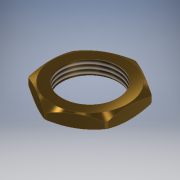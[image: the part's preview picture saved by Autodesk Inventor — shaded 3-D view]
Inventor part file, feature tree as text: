
AUTODESK INVENTOR PART (.ipt)
format: ipt  version: 2019 (Build 230136000, 136)  size: 170,496 bytes
history: native  units: mm
features: other x3, hole x1, chamfer x1
ambient origin geometry x8: Origin, YZ Plane, XZ Plane, XY Plane, X Axis, Y Axis, Z Axis, Center Point
bodies: Solid1 (feature_tree), Body (feature_tree)
feature tree (5):
  hole  "Hole Thread"  [1 undecoded]
  other  "Body Chamfer"
  chamfer  "Edge Chamfer"  Distance=10.0mm
  other  "Body Cross Section"
  other  "Body Chamfer Cross Section"
note: 1 required parameter value undecoded (feature->parameter linkage not recoverable at this tier; creation-order binding heuristic only, values carry confidence <= 0.55)
